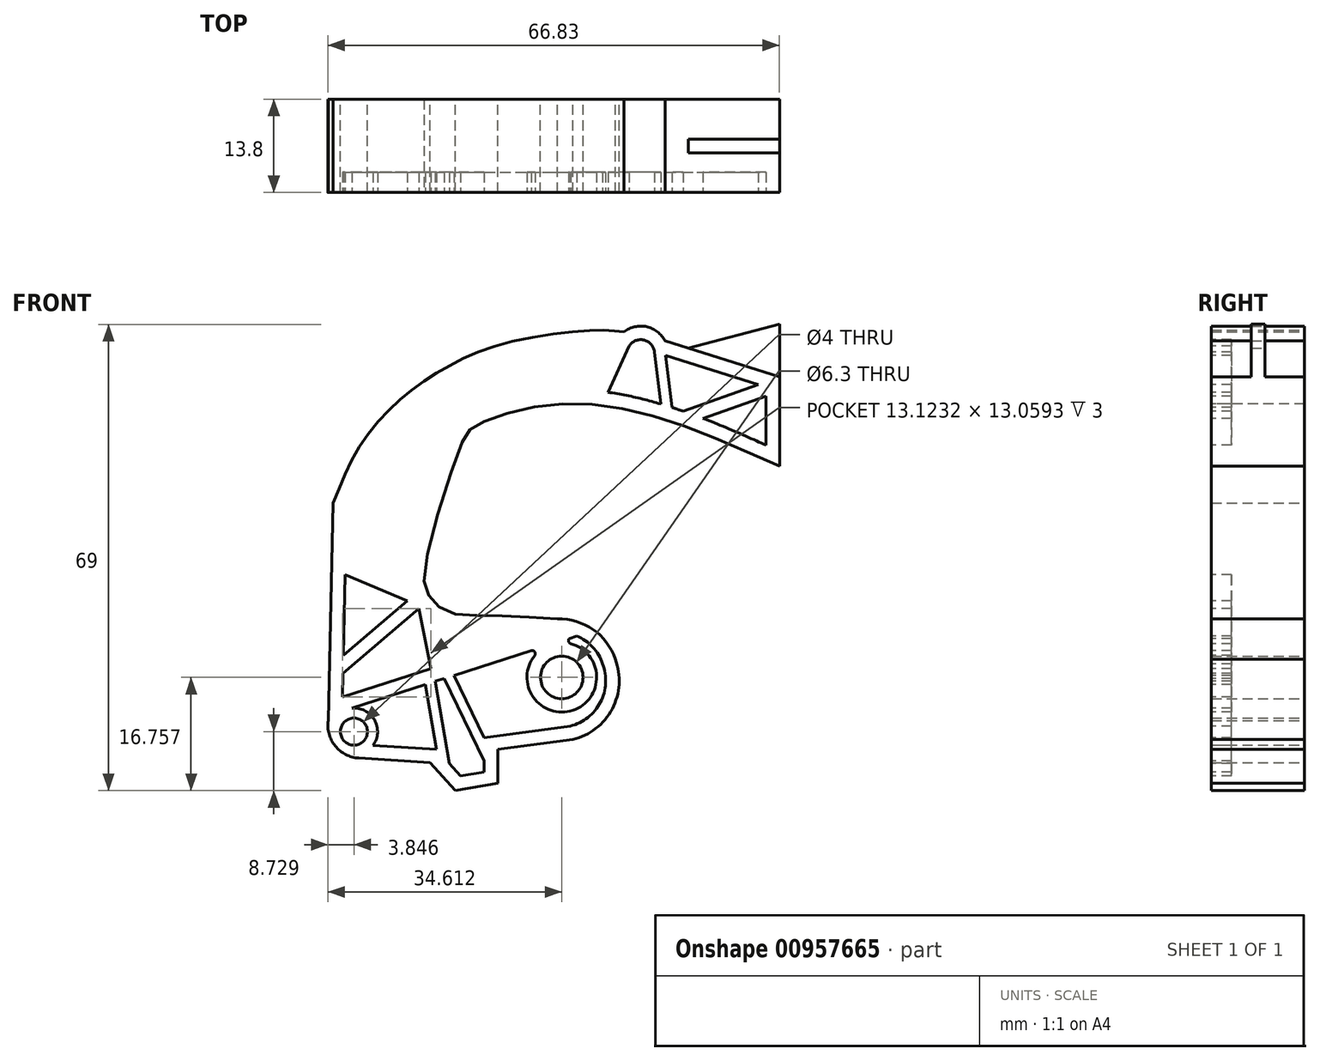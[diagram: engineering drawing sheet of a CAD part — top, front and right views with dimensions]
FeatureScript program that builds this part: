
annotation { "Feature Type Name" : "Feature", "Feature Type Description" : "" }
export const myFeature = defineFeature(function(context is Context, id is Id, definition is map)
    precondition{}
    {
        {
            var Q0;
            Q0=qCreatedBy(makeId("Front.planeOp"),FACE);
            var sketch = newSketch(context, id + "F0", { "sketchPlane" : qUnion([Q0])});
            skFitSpline(sketch, "E0", {"points": [v(45.38, 9.22) * mm, v(30.42, 15.45) * mm, v(17.62, 18.34) * mm, v(6.45, 17.43) * mm, v(0, 14.95) * mm, v(-1.61, 12.76) * mm, v(-7.13, -6.12) * mm, v(-6.5, -9.94) * mm, v(-3.88, -12.27) * mm, v(2.42, -12.91) * mm, v(12.53, -13.4) * mm], "startDerivative": vector(-110.03, 49.38) * mm, "endDerivative": vector(96.45, -6.27) * mm});
            skFitSpline(sketch, "E1", {"points": [v(22.37, 29.09) * mm, v(17.85, 29.33) * mm, v(4.41, 27.3) * mm, v(-4.5, 23.5) * mm, v(-11.29, 18.62) * mm, v(-17, 11.73) * mm, v(-20.68, 3.76) * mm], "startDerivative": vector(-31.63, 3.75) * mm, "endDerivative": vector(-19.47, -48.9) * mm});
            skLineSegment(sketch, "E2", {"start": v(-20.68, 3.76) * mm, "end": v(-21.4, -28.42) * mm});
            skLineSegment(sketch, "E3", {"start": v(-6.33, -34.64) * mm, "end": v(-16.9, -33.98) * mm});
            skArc(sketch, "E4", {"start": v(-21.4, -28.42) * mm, "mid": v(-20.37, -32.2) * mm, "end": v(-16.9, -33.98) * mm});
            skLineSegment(sketch, "E5", {"start": v(-6.33, -34.64) * mm, "end": v(-2.6, -38.8) * mm});
            skLineSegment(sketch, "E6", {"start": v(-2.6, -38.8) * mm, "end": v(3.69, -37.73) * mm});
            skLineSegment(sketch, "E7", {"start": v(3.69, -37.73) * mm, "end": v(3.69, -32.71) * mm});
            skCircle(sketch, "E8", {"center": v(13.16, -22.03) * mm, "radius": 3.15 * mm});
            skPoint(sketch, "E8.first.point", {"position": v(10.44, -20.45) * mm});
            skPoint(sketch, "E8.second.point", {"position": v(16.04, -23.32) * mm});
            skPoint(sketch, "E8.third.point", {"position": v(15.08, -24.53) * mm});
            skArc(sketch, "E9", {"start": v(21.08, -19.35) * mm, "mid": v(17.8, -14.95) * mm, "end": v(12.53, -13.4) * mm});
            skArc(sketch, "E10", {"start": v(14.79, -31.23) * mm, "mid": v(20.62, -26.7) * mm, "end": v(21.08, -19.35) * mm});
            skLineSegment(sketch, "E11", {"start": v(3.69, -32.71) * mm, "end": v(14.79, -31.23) * mm});
            skArc(sketch, "E12.0", {"start": v(18.44, -20.28) * mm, "mid": v(16.22, -17.27) * mm, "end": v(12.63, -16.2) * mm});
            skArc(sketch, "E12.1", {"start": v(14.14, -28.5) * mm, "mid": v(18.16, -25.37) * mm, "end": v(18.44, -20.28) * mm});
            skArc(sketch, "E13", {"start": v(12.63, -16.2) * mm, "mid": v(7.14, -23.12) * mm, "end": v(14.14, -28.5) * mm});
            skArc(sketch, "E14", {"start": v(28.45, 27.74) * mm, "mid": v(25.73, 29.85) * mm, "end": v(22.37, 29.09) * mm});
            skLineSegment(sketch, "E15", {"start": v(28.45, 27.74) * mm, "end": v(45.38, 22.41) * mm});
            skLineSegment(sketch, "E16", {"start": v(45.38, 22.41) * mm, "end": v(45.38, 9.22) * mm});
            skLineSegment(sketch, "E17", {"start": v(31.87, 26.66) * mm, "end": v(45.38, 30.21) * mm});
            skCircle(sketch, "E18", {"center": v(-17.6, -30.06) * mm, "radius": 2 * mm});
            skLineSegment(sketch, "E19", {"start": v(-21.45, -29) * mm, "end": v(-19.5, -29.43) * mm});
            skLineSegment(sketch, "E20", {"start": v(-21.28, -30.43) * mm, "end": v(-19.5, -30.7) * mm});
            skLineSegment(sketch, "E21", {"start": v(45.38, 30.21) * mm, "end": v(45.38, 22.41) * mm});
            skSolve(sketch);
        }
        {
            var Q0;
            Q0=makeQuery(id+"F0.imprint","IMPRINT",FACE,{"disambiguationData":[TD([[makeQuery(id+"F0.imprint","IMPRINT",EDGE,{"derivedFrom":sQuery(id+"F0.wireOp",EDGE,"E0")}),-1.0]])]});
            var Q1;
            Q1=makeQuery(id+"F0.imprint","IMPRINT",FACE,{"disambiguationData":[TD([[makeQuery(id+"F0.imprint","IMPRINT",EDGE,{"derivedFrom":sQuery(id+"F0.wireOp",EDGE,"E8")}),-1.0]])]});
            var Q2;
            {var subQ0=sQuery(id+"F0.wireOp",EDGE,"E19");Q2=makeQuery(id+"F0.imprint","IMPRINT",FACE,{"disambiguationData":[TD([[makeQuery(id+"F0.imprint","IMPRINT",EDGE,{"derivedFrom":subQ0}),-1.0]])]});}
            extrude(context, id + "F1", {"entities" : qUnion([Q0, Q1, Q2]), "endBound" : BoundingType.SYMMETRIC, "depth" : 13.8 * mm, "offsetDistance" : 25 * mm});
        }
        {
            var Q0;
            {var subQ2=sQuery(id+"F0.wireOp",EDGE,"E17");Q0=makeQuery(id+"F0.imprint","IMPRINT",FACE,{"disambiguationData":[TD([[makeQuery(id+"F0.imprint","IMPRINT",EDGE,{"derivedFrom":subQ2}),-1.0]])]});}
            extrude(context, id + "F2", {"entities" : qUnion([Q0]), "operationType" : NewBodyOperationType.ADD, "endBound" : BoundingType.SYMMETRIC, "depth" : 2 * mm, "offsetDistance" : 25 * mm});
        }
        {
            var Q0;
            Q0=makeQuery(id+"F1.opExtrude","CAP_FACE",FACE,{"disambiguationData":[OSD([sQuery(id+"F0.wireOp",EDGE,"E0"),sQuery(id+"F0.wireOp",EDGE,"E1"),sQuery(id+"F0.wireOp",EDGE,"E2"),sQuery(id+"F0.wireOp",EDGE,"E3"),sQuery(id+"F0.wireOp",EDGE,"E4"),sQuery(id+"F0.wireOp",EDGE,"E5"),sQuery(id+"F0.wireOp",EDGE,"E6"),sQuery(id+"F0.wireOp",EDGE,"E7"),sQuery(id+"F0.wireOp",EDGE,"E8"),sQuery(id+"F0.wireOp",EDGE,"E9"),sQuery(id+"F0.wireOp",EDGE,"E10"),sQuery(id+"F0.wireOp",EDGE,"E11"),sQuery(id+"F0.wireOp",EDGE,"E14"),sQuery(id+"F0.wireOp",EDGE,"E15"),sQuery(id+"F0.wireOp",EDGE,"E16"),sQuery(id+"F0.wireOp",EDGE,"E18")])],"isStart":false});
            var sketch = newSketch(context, id + "F3", { "sketchPlane" : qUnion([Q0])});
            skArc(sketch, "E22.0", {"start": v(19.2, -20.02) * mm, "mid": v(17.75, -17.55) * mm, "end": v(15.4, -15.91) * mm});
            skArc(sketch, "E22.1", {"start": v(14.42, -29.26) * mm, "mid": v(18.88, -25.71) * mm, "end": v(19.2, -20.02) * mm});
            skLineSegment(sketch, "E22.2", {"start": v(1.69, -30.96) * mm, "end": v(14.42, -29.26) * mm});
            skFitSpline(sketch, "E22.3", {"points": [v(22.13, 27.1) * mm, v(21.8, 27.14) * mm, v(21.17, 27.22) * mm, v(20.19, 27.3) * mm, v(19.07, 27.35) * mm, v(17.71, 27.33) * mm, v(16.03, 27.23) * mm, v(13.49, 27) * mm, v(10.65, 26.6) * mm, v(7.83, 26.07) * mm, v(6.14, 25.7) * mm, v(4.87, 25.36) * mm, v(3.67, 25.02) * mm, v(1.72, 24.36) * mm, v(-0.24, 23.52) * mm, v(-2.07, 22.59) * mm, v(-3.4, 21.84) * mm, v(-4.72, 21.05) * mm, v(-6.43, 19.94) * mm, v(-8.07, 18.75) * mm, v(-9.63, 17.44) * mm, v(-11.14, 16.04) * mm, v(-12.91, 14.11) * mm, v(-14.48, 12) * mm, v(-15.55, 10.26) * mm, v(-16.53, 8.44) * mm, v(-17.62, 6.05) * mm, v(-18.42, 4.04) * mm, v(-18.82, 3.02) * mm]});
            skArc(sketch, "E22.4", {"start": v(26.87, 26.14) * mm, "mid": v(25.3, 27.9) * mm, "end": v(23.13, 26.99) * mm});
            skLineSegment(sketch, "E22.5", {"start": v(26.87, 26.14) * mm, "end": v(26.87, 26.14) * mm});
            skLineSegment(sketch, "E22.6", {"start": v(43.38, 19.57) * mm, "end": v(43.38, 12.3) * mm});
            skLineSegment(sketch, "E22.7", {"start": v(-18.7, 3.36) * mm, "end": v(-18.74, 0.96) * mm});
            skLineSegment(sketch, "E22.9", {"start": v(-5.38, -32.7) * mm, "end": v(-14.77, -32.11) * mm});
            skLineSegment(sketch, "E22.10", {"start": v(-3.51, -34.79) * mm, "end": v(-1.85, -36.64) * mm});
            skLineSegment(sketch, "E22.11", {"start": v(-1.85, -36.64) * mm, "end": v(1.69, -36.04) * mm});
            skLineSegment(sketch, "E22.12", {"start": v(1.69, -36.04) * mm, "end": v(1.69, -34.4) * mm});
            skFitSpline(sketch, "E23.0", {"points": [v(46.2, 11.05) * mm, v(43.9, 12.08) * mm, v(39.3, 14.14) * mm, v(33.58, 16.48) * mm, v(29.06, 18.04) * mm, v(25.7, 19.01) * mm, v(22.35, 19.77) * mm, v(19, 20.27) * mm, v(15.66, 20.5) * mm, v(12.35, 20.41) * mm, v(9.67, 20.12) * mm, v(7.58, 19.75) * mm, v(6.04, 19.4) * mm, v(4.55, 18.99) * mm, v(3.14, 18.53) * mm, v(1.84, 18.05) * mm, v(0.86, 17.63) * mm, v(0.16, 17.3) * mm, v(-0.34, 17.06) * mm, v(-0.71, 16.85) * mm, v(-1, 16.69) * mm, v(-1.26, 16.52) * mm, v(-1.61, 16.28) * mm, v(-2.04, 15.92) * mm, v(-2.43, 15.49) * mm, v(-2.75, 15.02) * mm, v(-3.02, 14.53) * mm, v(-3.26, 14.01) * mm, v(-3.5, 13.44) * mm, v(-3.76, 12.78) * mm, v(-4.05, 12.02) * mm, v(-4.45, 10.9) * mm, v(-5, 9.32) * mm, v(-5.71, 7.19) * mm, v(-6.43, 4.92) * mm, v(-7.13, 2.6) * mm, v(-7.78, 0.29) * mm, v(-8.34, -1.91) * mm, v(-8.8, -3.93) * mm, v(-9.06, -5.4) * mm, v(-9.19, -6.45) * mm, v(-9.25, -7.42) * mm, v(-9.2, -8.51) * mm, v(-8.95, -9.51) * mm, v(-8.65, -10.21) * mm, v(-8.44, -10.6) * mm, v(-8.27, -10.89) * mm, v(-8.1, -11.15) * mm, v(-7.86, -11.49) * mm, v(-7.54, -11.9) * mm, v(-7.07, -12.45) * mm, v(-6.37, -13.11) * mm, v(-5.5, -13.7) * mm, v(-4.81, -14.05) * mm, v(-4.4, -14.22) * mm, v(-3.98, -14.37) * mm, v(-3.45, -14.52) * mm, v(-2.61, -14.7) * mm, v(-1.55, -14.82) * mm, v(-0.27, -14.89) * mm, v(0.82, -14.9) * mm, v(1.69, -14.9) * mm, v(2.34, -14.9) * mm, v(3, -14.92) * mm, v(3.9, -14.94) * mm, v(5.05, -14.98) * mm, v(6.94, -15.07) * mm, v(9.39, -15.2) * mm, v(11.4, -15.34) * mm, v(12.4, -15.4) * mm]});
            skArc(sketch, "E24.0", {"start": v(9.13, -18.83) * mm, "mid": v(14.79, -26.92) * mm, "end": v(14.48, -17.05) * mm});
            skArc(sketch, "E25.0", {"start": v(-14.77, -32.11) * mm, "mid": v(-14.56, -28.33) * mm, "end": v(-17.92, -26.58) * mm});
            skCircle(sketch, "E26.0", {"center": v(-17.6, -30.06) * mm, "radius": 2 * mm});
            skCircle(sketch, "E26.1", {"center": v(13.16, -22.03) * mm, "radius": 3.15 * mm});
            skLineSegment(sketch, "E27", {"start": v(-17.92, -26.58) * mm, "end": v(-7, -23.08) * mm});
            skLineSegment(sketch, "E28.0", {"start": v(-19.32, -24.92) * mm, "end": v(-6.2, -20.72) * mm});
            skArc(sketch, "E29", {"start": v(9.13, -18.83) * mm, "mid": v(9.16, -18.28) * mm, "end": v(8.65, -18.07) * mm});
            skArc(sketch, "E30", {"start": v(14.27, -16.27) * mm, "mid": v(14.17, -16.72) * mm, "end": v(14.48, -17.05) * mm});
            skLineSegment(sketch, "E31.trimOffspring", {"start": v(14.27, -16.27) * mm, "end": v(15.4, -15.91) * mm});
            skLineSegment(sketch, "E32", {"start": v(-19.25, -21.46) * mm, "end": v(-7.97, -11.87) * mm});
            skLineSegment(sketch, "E33", {"start": v(-6.19, 5.68) * mm, "end": v(-13.84, 12.84) * mm});
            skLineSegment(sketch, "E34.0", {"start": v(-19.19, -18.78) * mm, "end": v(-9.7, -10.71) * mm});
            skLineSegment(sketch, "E35.0", {"start": v(-9.7, -10.71) * mm, "end": v(-18.92, -6.87) * mm});
            skLineSegment(sketch, "E36.0", {"start": v(-18.74, 0.96) * mm, "end": v(-8.06, 4.7) * mm});
            skLineSegment(sketch, "E37.0", {"start": v(-8.06, 4.7) * mm, "end": v(-14.99, 11.17) * mm});
            skLineSegment(sketch, "E38.trimOffspring", {"start": v(-18.8, -1.18) * mm, "end": v(-18.87, -4.73) * mm});
            skLineSegment(sketch, "E39.trimOffspring", {"start": v(-18.92, -6.87) * mm, "end": v(-19.19, -18.78) * mm});
            skLineSegment(sketch, "E40.trimOffspring", {"start": v(-19.25, -21.46) * mm, "end": v(-19.32, -24.92) * mm});
            skFitSpline(sketch, "E41.trimOffspring", {"points": [v(46.2, 11.05) * mm, v(43.9, 12.08) * mm, v(39.3, 14.14) * mm, v(33.58, 16.48) * mm, v(29.06, 18.04) * mm, v(25.7, 19.01) * mm, v(22.35, 19.77) * mm, v(19, 20.27) * mm, v(15.66, 20.5) * mm, v(12.35, 20.41) * mm, v(9.67, 20.12) * mm, v(7.58, 19.75) * mm, v(6.04, 19.4) * mm, v(4.55, 18.99) * mm, v(3.14, 18.53) * mm, v(1.84, 18.05) * mm, v(0.86, 17.63) * mm, v(0.16, 17.3) * mm, v(-0.34, 17.06) * mm, v(-0.71, 16.85) * mm, v(-1, 16.69) * mm, v(-1.26, 16.52) * mm, v(-1.61, 16.28) * mm, v(-2.04, 15.92) * mm, v(-2.43, 15.49) * mm, v(-2.75, 15.02) * mm, v(-3.02, 14.53) * mm, v(-3.26, 14.01) * mm, v(-3.5, 13.44) * mm, v(-3.76, 12.78) * mm, v(-4.05, 12.02) * mm, v(-4.45, 10.9) * mm, v(-5, 9.32) * mm, v(-5.71, 7.19) * mm, v(-6.43, 4.92) * mm, v(-7.13, 2.6) * mm, v(-7.78, 0.29) * mm, v(-8.34, -1.91) * mm, v(-8.8, -3.93) * mm, v(-9.06, -5.4) * mm, v(-9.19, -6.45) * mm, v(-9.25, -7.42) * mm, v(-9.2, -8.51) * mm, v(-8.95, -9.51) * mm, v(-8.65, -10.21) * mm, v(-8.44, -10.6) * mm, v(-8.27, -10.89) * mm, v(-8.1, -11.15) * mm, v(-7.86, -11.49) * mm, v(-7.54, -11.9) * mm, v(-7.07, -12.45) * mm, v(-6.37, -13.11) * mm, v(-5.5, -13.7) * mm, v(-4.81, -14.05) * mm, v(-4.4, -14.22) * mm, v(-3.98, -14.37) * mm, v(-3.45, -14.52) * mm, v(-2.61, -14.7) * mm, v(-1.55, -14.82) * mm, v(-0.27, -14.89) * mm, v(0.82, -14.9) * mm, v(1.69, -14.9) * mm, v(2.34, -14.9) * mm, v(3, -14.92) * mm, v(3.9, -14.94) * mm, v(5.05, -14.98) * mm, v(6.94, -15.07) * mm, v(9.39, -15.2) * mm, v(11.4, -15.34) * mm, v(12.4, -15.4) * mm]});
            skFitSpline(sketch, "E42.trimOffspring", {"points": [v(46.2, 11.05) * mm, v(43.9, 12.08) * mm, v(39.3, 14.14) * mm, v(33.58, 16.48) * mm, v(29.06, 18.04) * mm, v(25.7, 19.01) * mm, v(22.35, 19.77) * mm, v(19, 20.27) * mm, v(15.66, 20.5) * mm, v(12.35, 20.41) * mm, v(9.67, 20.12) * mm, v(7.58, 19.75) * mm, v(6.04, 19.4) * mm, v(4.55, 18.99) * mm, v(3.14, 18.53) * mm, v(1.84, 18.05) * mm, v(0.86, 17.63) * mm, v(0.16, 17.3) * mm, v(-0.34, 17.06) * mm, v(-0.71, 16.85) * mm, v(-1, 16.69) * mm, v(-1.26, 16.52) * mm, v(-1.61, 16.28) * mm, v(-2.04, 15.92) * mm, v(-2.43, 15.49) * mm, v(-2.75, 15.02) * mm, v(-3.02, 14.53) * mm, v(-3.26, 14.01) * mm, v(-3.5, 13.44) * mm, v(-3.76, 12.78) * mm, v(-4.05, 12.02) * mm, v(-4.45, 10.9) * mm, v(-5, 9.32) * mm, v(-5.71, 7.19) * mm, v(-6.43, 4.92) * mm, v(-7.13, 2.6) * mm, v(-7.78, 0.29) * mm, v(-8.34, -1.91) * mm, v(-8.8, -3.93) * mm, v(-9.06, -5.4) * mm, v(-9.19, -6.45) * mm, v(-9.25, -7.42) * mm, v(-9.2, -8.51) * mm, v(-8.95, -9.51) * mm, v(-8.65, -10.21) * mm, v(-8.44, -10.6) * mm, v(-8.27, -10.89) * mm, v(-8.1, -11.15) * mm, v(-7.86, -11.49) * mm, v(-7.54, -11.9) * mm, v(-7.07, -12.45) * mm, v(-6.37, -13.11) * mm, v(-5.5, -13.7) * mm, v(-4.81, -14.05) * mm, v(-4.4, -14.22) * mm, v(-3.98, -14.37) * mm, v(-3.45, -14.52) * mm, v(-2.61, -14.7) * mm, v(-1.55, -14.82) * mm, v(-0.27, -14.89) * mm, v(0.82, -14.9) * mm, v(1.69, -14.9) * mm, v(2.34, -14.9) * mm, v(3, -14.92) * mm, v(3.9, -14.94) * mm, v(5.05, -14.98) * mm, v(6.94, -15.07) * mm, v(9.39, -15.2) * mm, v(11.4, -15.34) * mm, v(12.4, -15.4) * mm]});
            skFitSpline(sketch, "E43.trimOffspring", {"points": [v(22.13, 27.1) * mm, v(21.8, 27.14) * mm, v(21.17, 27.22) * mm, v(20.19, 27.3) * mm, v(19.07, 27.35) * mm, v(17.71, 27.33) * mm, v(16.03, 27.23) * mm, v(13.49, 27) * mm, v(10.65, 26.6) * mm, v(7.83, 26.07) * mm, v(6.14, 25.7) * mm, v(4.87, 25.36) * mm, v(3.67, 25.02) * mm, v(1.72, 24.36) * mm, v(-0.24, 23.52) * mm, v(-2.07, 22.59) * mm, v(-3.4, 21.84) * mm, v(-4.72, 21.05) * mm, v(-6.43, 19.94) * mm, v(-8.07, 18.75) * mm, v(-9.63, 17.44) * mm, v(-11.14, 16.04) * mm, v(-12.91, 14.11) * mm, v(-14.48, 12) * mm, v(-15.55, 10.26) * mm, v(-16.53, 8.44) * mm, v(-17.62, 6.05) * mm, v(-18.42, 4.04) * mm, v(-18.82, 3.02) * mm]});
            skLineSegment(sketch, "E44", {"start": v(-10.24, 16.87) * mm, "end": v(-2.83, 14.86) * mm});
            skLineSegment(sketch, "E45", {"start": v(1.81, 18.03) * mm, "end": v(1.81, 24.36) * mm});
            skLineSegment(sketch, "E46", {"start": v(8.24, 26.14) * mm, "end": v(14.33, 20.45) * mm});
            skLineSegment(sketch, "E47", {"start": v(18.09, 20.31) * mm, "end": v(21.25, 27.2) * mm});
            skLineSegment(sketch, "E48", {"start": v(28.55, 25.61) * mm, "end": v(29.48, 17.87) * mm});
            skLineSegment(sketch, "E49", {"start": v(34, 16.26) * mm, "end": v(43.38, 19.57) * mm});
            skLineSegment(sketch, "E50.0", {"start": v(-8.42, 18.44) * mm, "end": v(-1.28, 16.5) * mm});
            skLineSegment(sketch, "E51.0", {"start": v(-0.19, 17.13) * mm, "end": v(-0.19, 23.52) * mm});
            skLineSegment(sketch, "E52.0", {"start": v(5.87, 25.62) * mm, "end": v(11.55, 20.3) * mm});
            skLineSegment(sketch, "E53.0", {"start": v(19.97, 20.1) * mm, "end": v(23.15, 27.02) * mm});
            skLineSegment(sketch, "E54.0", {"start": v(26.87, 26.14) * mm, "end": v(27.8, 18.4) * mm});
            skLineSegment(sketch, "E55.0", {"start": v(31.04, 17.35) * mm, "end": v(42.27, 21.3) * mm});
            skFitSpline(sketch, "E56.trimOffspring", {"points": [v(46.2, 11.05) * mm, v(43.9, 12.08) * mm, v(39.3, 14.14) * mm, v(33.58, 16.48) * mm, v(29.06, 18.04) * mm, v(25.7, 19.01) * mm, v(22.35, 19.77) * mm, v(19, 20.27) * mm, v(15.66, 20.5) * mm, v(12.35, 20.41) * mm, v(9.67, 20.12) * mm, v(7.58, 19.75) * mm, v(6.04, 19.4) * mm, v(4.55, 18.99) * mm, v(3.14, 18.53) * mm, v(1.84, 18.05) * mm, v(0.86, 17.63) * mm, v(0.16, 17.3) * mm, v(-0.34, 17.06) * mm, v(-0.71, 16.85) * mm, v(-1, 16.69) * mm, v(-1.26, 16.52) * mm, v(-1.61, 16.28) * mm, v(-2.04, 15.92) * mm, v(-2.43, 15.49) * mm, v(-2.75, 15.02) * mm, v(-3.02, 14.53) * mm, v(-3.26, 14.01) * mm, v(-3.5, 13.44) * mm, v(-3.76, 12.78) * mm, v(-4.05, 12.02) * mm, v(-4.45, 10.9) * mm, v(-5, 9.32) * mm, v(-5.71, 7.19) * mm, v(-6.43, 4.92) * mm, v(-7.13, 2.6) * mm, v(-7.78, 0.29) * mm, v(-8.34, -1.91) * mm, v(-8.8, -3.93) * mm, v(-9.06, -5.4) * mm, v(-9.19, -6.45) * mm, v(-9.25, -7.42) * mm, v(-9.2, -8.51) * mm, v(-8.95, -9.51) * mm, v(-8.65, -10.21) * mm, v(-8.44, -10.6) * mm, v(-8.27, -10.89) * mm, v(-8.1, -11.15) * mm, v(-7.86, -11.49) * mm, v(-7.54, -11.9) * mm, v(-7.07, -12.45) * mm, v(-6.37, -13.11) * mm, v(-5.5, -13.7) * mm, v(-4.81, -14.05) * mm, v(-4.4, -14.22) * mm, v(-3.98, -14.37) * mm, v(-3.45, -14.52) * mm, v(-2.61, -14.7) * mm, v(-1.55, -14.82) * mm, v(-0.27, -14.89) * mm, v(0.82, -14.9) * mm, v(1.69, -14.9) * mm, v(2.34, -14.9) * mm, v(3, -14.92) * mm, v(3.9, -14.94) * mm, v(5.05, -14.98) * mm, v(6.94, -15.07) * mm, v(9.39, -15.2) * mm, v(11.4, -15.34) * mm, v(12.4, -15.4) * mm]});
            skFitSpline(sketch, "E57.trimOffspring", {"points": [v(46.2, 11.05) * mm, v(43.9, 12.08) * mm, v(39.3, 14.14) * mm, v(33.58, 16.48) * mm, v(29.06, 18.04) * mm, v(25.7, 19.01) * mm, v(22.35, 19.77) * mm, v(19, 20.27) * mm, v(15.66, 20.5) * mm, v(12.35, 20.41) * mm, v(9.67, 20.12) * mm, v(7.58, 19.75) * mm, v(6.04, 19.4) * mm, v(4.55, 18.99) * mm, v(3.14, 18.53) * mm, v(1.84, 18.05) * mm, v(0.86, 17.63) * mm, v(0.16, 17.3) * mm, v(-0.34, 17.06) * mm, v(-0.71, 16.85) * mm, v(-1, 16.69) * mm, v(-1.26, 16.52) * mm, v(-1.61, 16.28) * mm, v(-2.04, 15.92) * mm, v(-2.43, 15.49) * mm, v(-2.75, 15.02) * mm, v(-3.02, 14.53) * mm, v(-3.26, 14.01) * mm, v(-3.5, 13.44) * mm, v(-3.76, 12.78) * mm, v(-4.05, 12.02) * mm, v(-4.45, 10.9) * mm, v(-5, 9.32) * mm, v(-5.71, 7.19) * mm, v(-6.43, 4.92) * mm, v(-7.13, 2.6) * mm, v(-7.78, 0.29) * mm, v(-8.34, -1.91) * mm, v(-8.8, -3.93) * mm, v(-9.06, -5.4) * mm, v(-9.19, -6.45) * mm, v(-9.25, -7.42) * mm, v(-9.2, -8.51) * mm, v(-8.95, -9.51) * mm, v(-8.65, -10.21) * mm, v(-8.44, -10.6) * mm, v(-8.27, -10.89) * mm, v(-8.1, -11.15) * mm, v(-7.86, -11.49) * mm, v(-7.54, -11.9) * mm, v(-7.07, -12.45) * mm, v(-6.37, -13.11) * mm, v(-5.5, -13.7) * mm, v(-4.81, -14.05) * mm, v(-4.4, -14.22) * mm, v(-3.98, -14.37) * mm, v(-3.45, -14.52) * mm, v(-2.61, -14.7) * mm, v(-1.55, -14.82) * mm, v(-0.27, -14.89) * mm, v(0.82, -14.9) * mm, v(1.69, -14.9) * mm, v(2.34, -14.9) * mm, v(3, -14.92) * mm, v(3.9, -14.94) * mm, v(5.05, -14.98) * mm, v(6.94, -15.07) * mm, v(9.39, -15.2) * mm, v(11.4, -15.34) * mm, v(12.4, -15.4) * mm]});
            skLineSegment(sketch, "E58.trimOffspring", {"start": v(28.55, 25.61) * mm, "end": v(42.27, 21.3) * mm});
            skFitSpline(sketch, "E59.trimOffspring", {"points": [v(46.2, 11.05) * mm, v(43.9, 12.08) * mm, v(39.3, 14.14) * mm, v(33.58, 16.48) * mm, v(29.06, 18.04) * mm, v(25.7, 19.01) * mm, v(22.35, 19.77) * mm, v(19, 20.27) * mm, v(15.66, 20.5) * mm, v(12.35, 20.41) * mm, v(9.67, 20.12) * mm, v(7.58, 19.75) * mm, v(6.04, 19.4) * mm, v(4.55, 18.99) * mm, v(3.14, 18.53) * mm, v(1.84, 18.05) * mm, v(0.86, 17.63) * mm, v(0.16, 17.3) * mm, v(-0.34, 17.06) * mm, v(-0.71, 16.85) * mm, v(-1, 16.69) * mm, v(-1.26, 16.52) * mm, v(-1.61, 16.28) * mm, v(-2.04, 15.92) * mm, v(-2.43, 15.49) * mm, v(-2.75, 15.02) * mm, v(-3.02, 14.53) * mm, v(-3.26, 14.01) * mm, v(-3.5, 13.44) * mm, v(-3.76, 12.78) * mm, v(-4.05, 12.02) * mm, v(-4.45, 10.9) * mm, v(-5, 9.32) * mm, v(-5.71, 7.19) * mm, v(-6.43, 4.92) * mm, v(-7.13, 2.6) * mm, v(-7.78, 0.29) * mm, v(-8.34, -1.91) * mm, v(-8.8, -3.93) * mm, v(-9.06, -5.4) * mm, v(-9.19, -6.45) * mm, v(-9.25, -7.42) * mm, v(-9.2, -8.51) * mm, v(-8.95, -9.51) * mm, v(-8.65, -10.21) * mm, v(-8.44, -10.6) * mm, v(-8.27, -10.89) * mm, v(-8.1, -11.15) * mm, v(-7.86, -11.49) * mm, v(-7.54, -11.9) * mm, v(-7.07, -12.45) * mm, v(-6.37, -13.11) * mm, v(-5.5, -13.7) * mm, v(-4.81, -14.05) * mm, v(-4.4, -14.22) * mm, v(-3.98, -14.37) * mm, v(-3.45, -14.52) * mm, v(-2.61, -14.7) * mm, v(-1.55, -14.82) * mm, v(-0.27, -14.89) * mm, v(0.82, -14.9) * mm, v(1.69, -14.9) * mm, v(2.34, -14.9) * mm, v(3, -14.92) * mm, v(3.9, -14.94) * mm, v(5.05, -14.98) * mm, v(6.94, -15.07) * mm, v(9.39, -15.2) * mm, v(11.4, -15.34) * mm, v(12.4, -15.4) * mm]});
            skFitSpline(sketch, "E60.trimOffspring", {"points": [v(46.2, 11.05) * mm, v(43.9, 12.08) * mm, v(39.3, 14.14) * mm, v(33.58, 16.48) * mm, v(29.06, 18.04) * mm, v(25.7, 19.01) * mm, v(22.35, 19.77) * mm, v(19, 20.27) * mm, v(15.66, 20.5) * mm, v(12.35, 20.41) * mm, v(9.67, 20.12) * mm, v(7.58, 19.75) * mm, v(6.04, 19.4) * mm, v(4.55, 18.99) * mm, v(3.14, 18.53) * mm, v(1.84, 18.05) * mm, v(0.86, 17.63) * mm, v(0.16, 17.3) * mm, v(-0.34, 17.06) * mm, v(-0.71, 16.85) * mm, v(-1, 16.69) * mm, v(-1.26, 16.52) * mm, v(-1.61, 16.28) * mm, v(-2.04, 15.92) * mm, v(-2.43, 15.49) * mm, v(-2.75, 15.02) * mm, v(-3.02, 14.53) * mm, v(-3.26, 14.01) * mm, v(-3.5, 13.44) * mm, v(-3.76, 12.78) * mm, v(-4.05, 12.02) * mm, v(-4.45, 10.9) * mm, v(-5, 9.32) * mm, v(-5.71, 7.19) * mm, v(-6.43, 4.92) * mm, v(-7.13, 2.6) * mm, v(-7.78, 0.29) * mm, v(-8.34, -1.91) * mm, v(-8.8, -3.93) * mm, v(-9.06, -5.4) * mm, v(-9.19, -6.45) * mm, v(-9.25, -7.42) * mm, v(-9.2, -8.51) * mm, v(-8.95, -9.51) * mm, v(-8.65, -10.21) * mm, v(-8.44, -10.6) * mm, v(-8.27, -10.89) * mm, v(-8.1, -11.15) * mm, v(-7.86, -11.49) * mm, v(-7.54, -11.9) * mm, v(-7.07, -12.45) * mm, v(-6.37, -13.11) * mm, v(-5.5, -13.7) * mm, v(-4.81, -14.05) * mm, v(-4.4, -14.22) * mm, v(-3.98, -14.37) * mm, v(-3.45, -14.52) * mm, v(-2.61, -14.7) * mm, v(-1.55, -14.82) * mm, v(-0.27, -14.89) * mm, v(0.82, -14.9) * mm, v(1.69, -14.9) * mm, v(2.34, -14.9) * mm, v(3, -14.92) * mm, v(3.9, -14.94) * mm, v(5.05, -14.98) * mm, v(6.94, -15.07) * mm, v(9.39, -15.2) * mm, v(11.4, -15.34) * mm, v(12.4, -15.4) * mm]});
            skFitSpline(sketch, "E61.trimOffspring", {"points": [v(22.13, 27.1) * mm, v(21.8, 27.14) * mm, v(21.17, 27.22) * mm, v(20.19, 27.3) * mm, v(19.07, 27.35) * mm, v(17.71, 27.33) * mm, v(16.03, 27.23) * mm, v(13.49, 27) * mm, v(10.65, 26.6) * mm, v(7.83, 26.07) * mm, v(6.14, 25.7) * mm, v(4.87, 25.36) * mm, v(3.67, 25.02) * mm, v(1.72, 24.36) * mm, v(-0.24, 23.52) * mm, v(-2.07, 22.59) * mm, v(-3.4, 21.84) * mm, v(-4.72, 21.05) * mm, v(-6.43, 19.94) * mm, v(-8.07, 18.75) * mm, v(-9.63, 17.44) * mm, v(-11.14, 16.04) * mm, v(-12.91, 14.11) * mm, v(-14.48, 12) * mm, v(-15.55, 10.26) * mm, v(-16.53, 8.44) * mm, v(-17.62, 6.05) * mm, v(-18.42, 4.04) * mm, v(-18.82, 3.02) * mm]});
            skFitSpline(sketch, "E62.trimOffspring", {"points": [v(22.13, 27.1) * mm, v(21.8, 27.14) * mm, v(21.17, 27.22) * mm, v(20.19, 27.3) * mm, v(19.07, 27.35) * mm, v(17.71, 27.33) * mm, v(16.03, 27.23) * mm, v(13.49, 27) * mm, v(10.65, 26.6) * mm, v(7.83, 26.07) * mm, v(6.14, 25.7) * mm, v(4.87, 25.36) * mm, v(3.67, 25.02) * mm, v(1.72, 24.36) * mm, v(-0.24, 23.52) * mm, v(-2.07, 22.59) * mm, v(-3.4, 21.84) * mm, v(-4.72, 21.05) * mm, v(-6.43, 19.94) * mm, v(-8.07, 18.75) * mm, v(-9.63, 17.44) * mm, v(-11.14, 16.04) * mm, v(-12.91, 14.11) * mm, v(-14.48, 12) * mm, v(-15.55, 10.26) * mm, v(-16.53, 8.44) * mm, v(-17.62, 6.05) * mm, v(-18.42, 4.04) * mm, v(-18.82, 3.02) * mm]});
            skFitSpline(sketch, "E63.trimOffspring", {"points": [v(46.2, 11.05) * mm, v(43.9, 12.08) * mm, v(39.3, 14.14) * mm, v(33.58, 16.48) * mm, v(29.06, 18.04) * mm, v(25.7, 19.01) * mm, v(22.35, 19.77) * mm, v(19, 20.27) * mm, v(15.66, 20.5) * mm, v(12.35, 20.41) * mm, v(9.67, 20.12) * mm, v(7.58, 19.75) * mm, v(6.04, 19.4) * mm, v(4.55, 18.99) * mm, v(3.14, 18.53) * mm, v(1.84, 18.05) * mm, v(0.86, 17.63) * mm, v(0.16, 17.3) * mm, v(-0.34, 17.06) * mm, v(-0.71, 16.85) * mm, v(-1, 16.69) * mm, v(-1.26, 16.52) * mm, v(-1.61, 16.28) * mm, v(-2.04, 15.92) * mm, v(-2.43, 15.49) * mm, v(-2.75, 15.02) * mm, v(-3.02, 14.53) * mm, v(-3.26, 14.01) * mm, v(-3.5, 13.44) * mm, v(-3.76, 12.78) * mm, v(-4.05, 12.02) * mm, v(-4.45, 10.9) * mm, v(-5, 9.32) * mm, v(-5.71, 7.19) * mm, v(-6.43, 4.92) * mm, v(-7.13, 2.6) * mm, v(-7.78, 0.29) * mm, v(-8.34, -1.91) * mm, v(-8.8, -3.93) * mm, v(-9.06, -5.4) * mm, v(-9.19, -6.45) * mm, v(-9.25, -7.42) * mm, v(-9.2, -8.51) * mm, v(-8.95, -9.51) * mm, v(-8.65, -10.21) * mm, v(-8.44, -10.6) * mm, v(-8.27, -10.89) * mm, v(-8.1, -11.15) * mm, v(-7.86, -11.49) * mm, v(-7.54, -11.9) * mm, v(-7.07, -12.45) * mm, v(-6.37, -13.11) * mm, v(-5.5, -13.7) * mm, v(-4.81, -14.05) * mm, v(-4.4, -14.22) * mm, v(-3.98, -14.37) * mm, v(-3.45, -14.52) * mm, v(-2.61, -14.7) * mm, v(-1.55, -14.82) * mm, v(-0.27, -14.89) * mm, v(0.82, -14.9) * mm, v(1.69, -14.9) * mm, v(2.34, -14.9) * mm, v(3, -14.92) * mm, v(3.9, -14.94) * mm, v(5.05, -14.98) * mm, v(6.94, -15.07) * mm, v(9.39, -15.2) * mm, v(11.4, -15.34) * mm, v(12.4, -15.4) * mm]});
            skFitSpline(sketch, "E64.trimOffspring", {"points": [v(46.2, 11.05) * mm, v(43.9, 12.08) * mm, v(39.3, 14.14) * mm, v(33.58, 16.48) * mm, v(29.06, 18.04) * mm, v(25.7, 19.01) * mm, v(22.35, 19.77) * mm, v(19, 20.27) * mm, v(15.66, 20.5) * mm, v(12.35, 20.41) * mm, v(9.67, 20.12) * mm, v(7.58, 19.75) * mm, v(6.04, 19.4) * mm, v(4.55, 18.99) * mm, v(3.14, 18.53) * mm, v(1.84, 18.05) * mm, v(0.86, 17.63) * mm, v(0.16, 17.3) * mm, v(-0.34, 17.06) * mm, v(-0.71, 16.85) * mm, v(-1, 16.69) * mm, v(-1.26, 16.52) * mm, v(-1.61, 16.28) * mm, v(-2.04, 15.92) * mm, v(-2.43, 15.49) * mm, v(-2.75, 15.02) * mm, v(-3.02, 14.53) * mm, v(-3.26, 14.01) * mm, v(-3.5, 13.44) * mm, v(-3.76, 12.78) * mm, v(-4.05, 12.02) * mm, v(-4.45, 10.9) * mm, v(-5, 9.32) * mm, v(-5.71, 7.19) * mm, v(-6.43, 4.92) * mm, v(-7.13, 2.6) * mm, v(-7.78, 0.29) * mm, v(-8.34, -1.91) * mm, v(-8.8, -3.93) * mm, v(-9.06, -5.4) * mm, v(-9.19, -6.45) * mm, v(-9.25, -7.42) * mm, v(-9.2, -8.51) * mm, v(-8.95, -9.51) * mm, v(-8.65, -10.21) * mm, v(-8.44, -10.6) * mm, v(-8.27, -10.89) * mm, v(-8.1, -11.15) * mm, v(-7.86, -11.49) * mm, v(-7.54, -11.9) * mm, v(-7.07, -12.45) * mm, v(-6.37, -13.11) * mm, v(-5.5, -13.7) * mm, v(-4.81, -14.05) * mm, v(-4.4, -14.22) * mm, v(-3.98, -14.37) * mm, v(-3.45, -14.52) * mm, v(-2.61, -14.7) * mm, v(-1.55, -14.82) * mm, v(-0.27, -14.89) * mm, v(0.82, -14.9) * mm, v(1.69, -14.9) * mm, v(2.34, -14.9) * mm, v(3, -14.92) * mm, v(3.9, -14.94) * mm, v(5.05, -14.98) * mm, v(6.94, -15.07) * mm, v(9.39, -15.2) * mm, v(11.4, -15.34) * mm, v(12.4, -15.4) * mm]});
            skFitSpline(sketch, "E65.trimOffspring", {"points": [v(22.13, 27.1) * mm, v(21.8, 27.14) * mm, v(21.17, 27.22) * mm, v(20.19, 27.3) * mm, v(19.07, 27.35) * mm, v(17.71, 27.33) * mm, v(16.03, 27.23) * mm, v(13.49, 27) * mm, v(10.65, 26.6) * mm, v(7.83, 26.07) * mm, v(6.14, 25.7) * mm, v(4.87, 25.36) * mm, v(3.67, 25.02) * mm, v(1.72, 24.36) * mm, v(-0.24, 23.52) * mm, v(-2.07, 22.59) * mm, v(-3.4, 21.84) * mm, v(-4.72, 21.05) * mm, v(-6.43, 19.94) * mm, v(-8.07, 18.75) * mm, v(-9.63, 17.44) * mm, v(-11.14, 16.04) * mm, v(-12.91, 14.11) * mm, v(-14.48, 12) * mm, v(-15.55, 10.26) * mm, v(-16.53, 8.44) * mm, v(-17.62, 6.05) * mm, v(-18.42, 4.04) * mm, v(-18.82, 3.02) * mm]});
            skLineSegment(sketch, "E66", {"start": v(1.69, -30.96) * mm, "end": v(-2.79, -21.73) * mm});
            skLineSegment(sketch, "E67", {"start": v(-5.38, -32.7) * mm, "end": v(-7, -23.08) * mm});
            skLineSegment(sketch, "E68.0", {"start": v(1.69, -34.4) * mm, "end": v(-4.23, -22.2) * mm});
            skLineSegment(sketch, "E68.1", {"start": v(-3.51, -34.79) * mm, "end": v(-5.56, -22.62) * mm});
            skLineSegment(sketch, "E69.trimOffspring", {"start": v(-5.56, -22.62) * mm, "end": v(-4.23, -22.2) * mm});
            skLineSegment(sketch, "E70.trimOffspring", {"start": v(-2.79, -21.73) * mm, "end": v(8.65, -18.07) * mm});
            skLineSegment(sketch, "E71", {"start": v(-4.28, -20.11) * mm, "end": v(-5.58, -13.64) * mm});
            skLineSegment(sketch, "E72.0", {"start": v(-6.2, -20.72) * mm, "end": v(-7.97, -11.87) * mm});
            skLineSegment(sketch, "E73.trimOffspring", {"start": v(-4.28, -20.11) * mm, "end": v(10.76, -15.3) * mm});
            skLineSegment(sketch, "E74", {"start": v(-18.8, -1.18) * mm, "end": v(-7.02, 2.95) * mm});
            skLineSegment(sketch, "E75", {"start": v(-18.87, -4.73) * mm, "end": v(-9.1, -8.8) * mm});
            skSolve(sketch);
        }
        {
            var Q0;
            Q0=makeQuery(id+"F3.imprint","IMPRINT",FACE,{"disambiguationData":[TD([[makeQuery(id+"F3.imprint","IMPRINT",EDGE,{"derivedFrom":sQuery(id+"F3.wireOp",EDGE,"E22.9")}),-1.0]])]});
            var Q1;
            Q1=makeQuery(id+"F3.imprint","IMPRINT",FACE,{"disambiguationData":[TD([[makeQuery(id+"F3.imprint","IMPRINT",EDGE,{"derivedFrom":sQuery(id+"F3.wireOp",EDGE,"E22.10")}),1.0]])]});
            var Q2;
            Q2=makeQuery(id+"F3.imprint","IMPRINT",FACE,{"disambiguationData":[TD([[makeQuery(id+"F3.imprint","IMPRINT",EDGE,{"derivedFrom":sQuery(id+"F3.wireOp",EDGE,"E22.0")}),1.0]])]});
            var Q3;
            Q3=makeQuery(id+"F3.imprint","IMPRINT",FACE,{"disambiguationData":[TD([[makeQuery(id+"F3.imprint","IMPRINT",EDGE,{"derivedFrom":sQuery(id+"F3.wireOp",EDGE,"E41.trimOffspring")}),-1.0]])]});
            var Q4;
            Q4=makeQuery(id+"F3.imprint","IMPRINT",FACE,{"disambiguationData":[TD([[makeQuery(id+"F3.imprint","IMPRINT",EDGE,{"derivedFrom":sQuery(id+"F3.wireOp",EDGE,"E28.0")}),1.0]])]});
            var Q5;
            Q5=makeQuery(id+"F3.imprint","IMPRINT",FACE,{"disambiguationData":[TD([[makeQuery(id+"F3.imprint","IMPRINT",EDGE,{"derivedFrom":sQuery(id+"F3.wireOp",EDGE,"E34.0")}),1.0]])]});
            var Q6;
            Q6=makeQuery(id+"F3.imprint","IMPRINT",FACE,{"disambiguationData":[TD([[makeQuery(id+"F3.imprint","IMPRINT",EDGE,{"derivedFrom":sQuery(id+"F3.wireOp",EDGE,"E22.7")}),1.0]])]});
            var Q7;
            Q7=makeQuery(id+"F3.imprint","IMPRINT",FACE,{"disambiguationData":[TD([[makeQuery(id+"F3.imprint","IMPRINT",EDGE,{"derivedFrom":sQuery(id+"F3.wireOp",EDGE,"E33")}),-1.0]])]});
            var Q8;
            Q8=makeQuery(id+"F3.imprint","IMPRINT",FACE,{"disambiguationData":[TD([[makeQuery(id+"F3.imprint","IMPRINT",EDGE,{"derivedFrom":sQuery(id+"F3.wireOp",EDGE,"E50.0")}),1.0]])]});
            var Q9;
            Q9=makeQuery(id+"F3.imprint","IMPRINT",FACE,{"disambiguationData":[TD([[makeQuery(id+"F3.imprint","IMPRINT",EDGE,{"derivedFrom":sQuery(id+"F3.wireOp",EDGE,"E45")}),-1.0]])]});
            var Q10;
            {var subQ1=sQuery(id+"F3.wireOp",EDGE,"E22.5");Q10=makeQuery(id+"F3.imprint","IMPRINT",FACE,{"disambiguationData":[TD([[makeQuery(id+"F3.imprint","IMPRINT",EDGE,{"derivedFrom":subQ1}),-1.0]])]});}
            var Q11;
            Q11=makeQuery(id+"F3.imprint","IMPRINT",FACE,{"disambiguationData":[TD([[makeQuery(id+"F3.imprint","IMPRINT",EDGE,{"derivedFrom":sQuery(id+"F3.wireOp",EDGE,"E48")}),1.0]])]});
            var Q12;
            {var subQ0=sQuery(id+"F3.wireOp",EDGE,"E22.6");Q12=makeQuery(id+"F3.imprint","IMPRINT",FACE,{"disambiguationData":[TD([[makeQuery(id+"F3.imprint","IMPRINT",EDGE,{"derivedFrom":subQ0}),-1.0]])]});}
            extrude(context, id + "F4", {"entities" : qUnion([Q0, Q1, Q2, Q3, Q4, Q5, Q6, Q7, Q8, Q9, Q10, Q11, Q12]), "operationType" : NewBodyOperationType.REMOVE, "oppositeDirection" : true, "depth" : 3 * mm, "offsetDistance" : 25 * mm});
        }
    });
